# Revit family: ITK_Осветительная панель_Винтовое крепление_1U_IP20
name_source: partatom
category: Обобщенные модели
units: mm (PartAtom-declared; Revit-internal decimal feet)

## family parameters
Всегда вертикально = Да
Может служить основой для арматурных стержней = Нет
На основе рабочей плоскости = Нет
Общий = Нет
При загрузке вырезать с полостями = Нет
Размер круглого соединителя = Использовать диаметр
Тип детали = Нормальный
Точка расчета площади = Нет

## types (1)
- LE35-1U1
    ADSK_URL страницы изделия = https://www.itk-group.ru
    ADSK_Версия Revit = 2019
    ADSK_Версия семейства = 1.0
    ADSK_Группирование = I. ЩИТЫ И ПУЛЬТЫ
    ADSK_Единица измерения = шт
    ADSK_Завод-изготовитель = IEK
    ADSK_Классификация нагрузок = Прочее
    ADSK_Код изделия = LE35-1U1
    ADSK_Количество фаз = 1
    ADSK_Количество фаз числовое = 1
    ADSK_Коэффициент мощности = 1
    ADSK_Масса = 0.5
    ADSK_Материал наименование = Листовая сталь, пластик
    ADSK_Наименование = ITK 19" осветительная панель, 1U, с ручным вкл., серая
    ADSK_Напряжение = 230 В
    ADSK_Номинальная мощность = 4 Вт
    ADSK_Полная мощность = 4 В·А
    ADSK_Ток = 0 А
    IEK_URL = https://www.itk-group.ru
    IEK_Описание = Совместимы со всеми 19" шкафами и стойками ITK.
Современный привлекательный дизайн и продуманная конструкция.
Удобны в монтаже и эксплуатации.
Выключатель на корпусе панели.
Кабель электропитания в комплекте, 2 м, евровилка.
Соответствие российским и международным стандартам.
Все осветительные панели идут с крепежом.
Поставляются в качественной компактной упаковке.
    IEK_Цена за единицу = 2854.72
    KSI_CMa_Строительные материалы = 10.03.02.06
    KSI_CPr_Строительные изделия = 61.1.04.08
    URL = https://www.iek.ru
    Высота = 45 мм
    Глубина = 26 мм
    Изготовитель = ITK
    Материал = Окраска - RAL 7035
    Тип монтажа = Винтовое крепление
    Ширина = 483 мм
